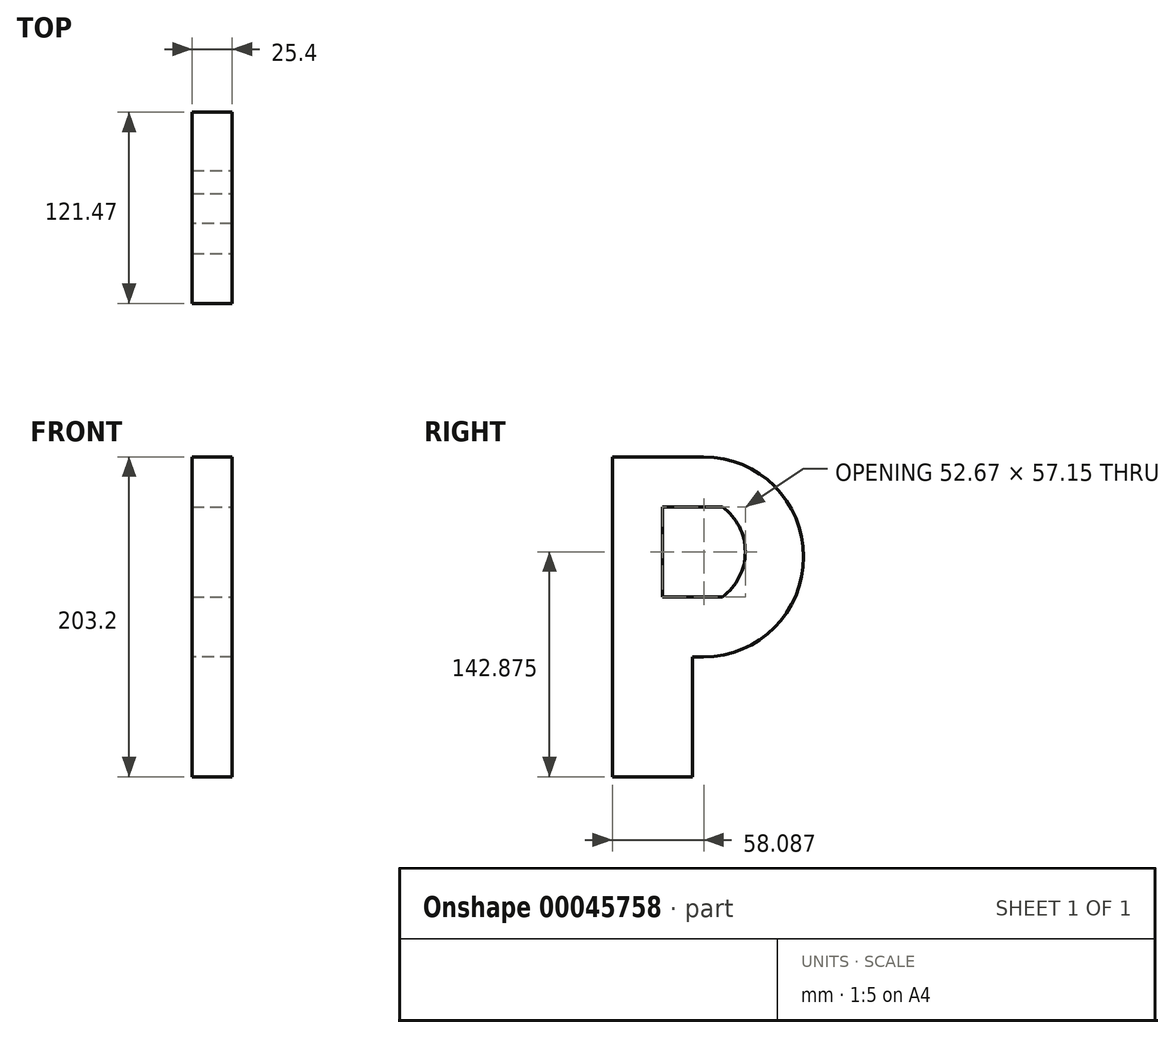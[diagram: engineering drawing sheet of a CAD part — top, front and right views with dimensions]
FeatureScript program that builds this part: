
annotation { "Feature Type Name" : "Feature", "Feature Type Description" : "" }
export const myFeature = defineFeature(function(context is Context, id is Id, definition is map)
    precondition{}
    {
        {
            var Q0;
            Q0=qCreatedBy(makeId("Right.planeOp"),FACE);
            var sketch = newSketch(context, id + "F0", { "sketchPlane" : qUnion([Q0])});
            skLineSegment(sketch, "E0", {"start": v(0, -76.2) * mm, "end": v(0, 127) * mm});
            skLineSegment(sketch, "E1", {"start": v(0, 127) * mm, "end": v(29.3, 127) * mm});
            skLineSegment(sketch, "E2", {"start": v(0, -76.2) * mm, "end": v(50.8, -76.2) * mm});
            skLineSegment(sketch, "E3", {"start": v(50.8, -76.2) * mm, "end": v(50.8, 0) * mm});
            skLineSegment(sketch, "E4", {"start": v(50.8, 0) * mm, "end": v(57.97, 0) * mm});
            skLineSegment(sketch, "E5", {"start": v(29.3, 127) * mm, "end": v(57.97, 127) * mm});
            skArc(sketch, "E6", {"start": v(57.97, 127) * mm, "mid": v(121.47, 63.5) * mm, "end": v(57.97, 0) * mm});
            skSolve(sketch);
        }
        {
            var Q0;
            Q0 = qSketchRegion(id + "F0", true);
            extrude(context, id + "F1", {"entities" : qUnion([Q0]), "depth" : 25.4 * mm});
        }
        {
            var Q0;
            Q0=makeQuery(id+"F1.opExtrude","CAP_FACE",FACE,{"disambiguationData":[OSD([sQuery(id+"F0.wireOp",EDGE,"E0"),sQuery(id+"F0.wireOp",EDGE,"E1"),sQuery(id+"F0.wireOp",EDGE,"E2"),sQuery(id+"F0.wireOp",EDGE,"E3"),sQuery(id+"F0.wireOp",EDGE,"E4"),sQuery(id+"F0.wireOp",EDGE,"E5"),sQuery(id+"F0.wireOp",EDGE,"E6")])],"isStart":false});
            var sketch = newSketch(context, id + "F2", { "sketchPlane" : qUnion([Q0])});
            skLineSegment(sketch, "E7", {"start": v(50.8, 38.1) * mm, "end": v(31.75, 38.1) * mm});
            skLineSegment(sketch, "E8", {"start": v(31.75, 38.1) * mm, "end": v(31.75, 95.25) * mm});
            skLineSegment(sketch, "E9", {"start": v(31.75, 95.25) * mm, "end": v(69.85, 95.25) * mm});
            skLineSegment(sketch, "E10", {"start": v(50.8, 38.1) * mm, "end": v(69.8, 38.1) * mm});
            skArc(sketch, "E11", {"start": v(69.8, 38.1) * mm, "mid": v(84.42, 66.66) * mm, "end": v(69.85, 95.25) * mm});
            skSolve(sketch);
        }
        {
            var Q0;
            Q0 = qSketchRegion(id + "F2", true);
            extrude(context, id + "F3", {"entities" : qUnion([Q0]), "operationType" : NewBodyOperationType.REMOVE, "oppositeDirection" : true, "depth" : 25.4 * mm});
        }
    });
